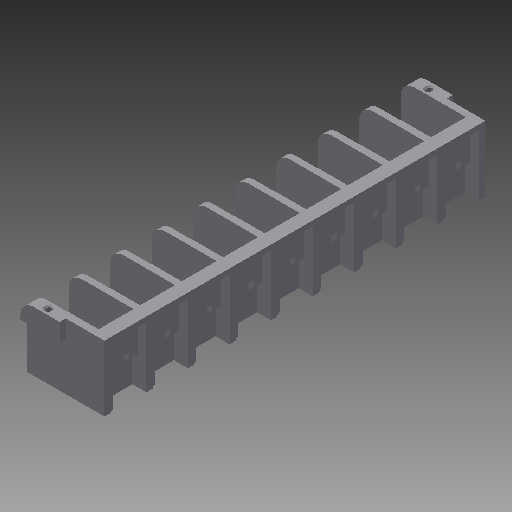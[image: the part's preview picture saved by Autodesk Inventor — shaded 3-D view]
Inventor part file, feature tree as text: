
AUTODESK INVENTOR PART (.ipt)
format: ipt  version: 2017 (Build 210142000, 142)  size: 476,160 bytes
history: native  units: in
note: dims shown in document units (in); Inventor stores cm internally (conversion verified against a paired STEP export)
features: sketch x2, other x1
ambient origin geometry x8: Origin, YZ Plane, XZ Plane, XY Plane, X Axis, Y Axis, Z Axis, Center Point
bodies: Solid1 (feature_tree)
feature tree (3):
  other  "abl2rem24150k"
  sketch  "Sketch1"
  sketch  "Sketch2"
